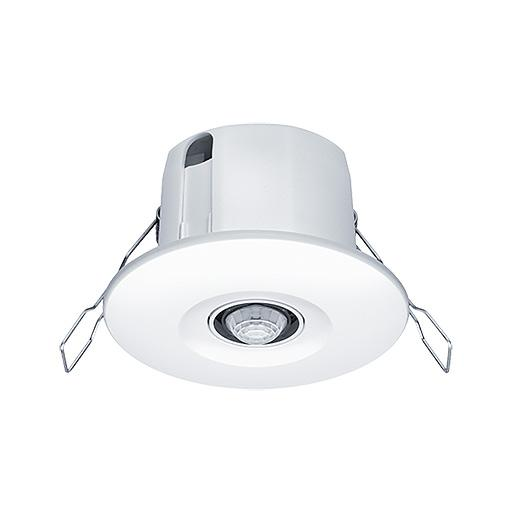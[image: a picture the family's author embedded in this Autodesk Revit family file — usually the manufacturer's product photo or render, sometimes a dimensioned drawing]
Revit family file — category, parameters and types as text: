
# Revit family: Zumtobel basicDIM ILD G2 SRC 20 4DPI WDA
name_source: partatom
category: Lighting Devices
units: mm (PartAtom-declared; Revit-internal decimal feet)

## family parameters
Cut with Voids When Loaded = Yes
Host = Face
Maintain Annotation Orientation = No
OmniClass Number = 23.85.80.11.27
OmniClass Title = Lighting Controls
Part Type = Normal
Room Calculation Point = Yes
Round Connector Dimension = Use Diameter
Shared = No

## types (1)
- basicDIM ILD G2 SRC 20 4DPI WDA WH
    Assembly Code = D5030800
    Default Elevation = 0 mm  [stored 0 ft]
    Description = Motion Sensor
    Manufacturer = Zumtobel Lighting
    Material-Housing = ZG-Lighting Fixtures-Plastic-White_RGB 255 255 255
    Model = 28004641
    Type Image = basicDIM ILD G2 SRC 20 4DPI.jpg
    URL = https://www.zumtobel.com

note: [stored X ft] marks values corroborated as IEEE doubles in the binary element streams (Revit-internal decimal feet)

## geometry (parser evidence)
native form markers: Sweep x2
no freeform markers — native parametric forms only
